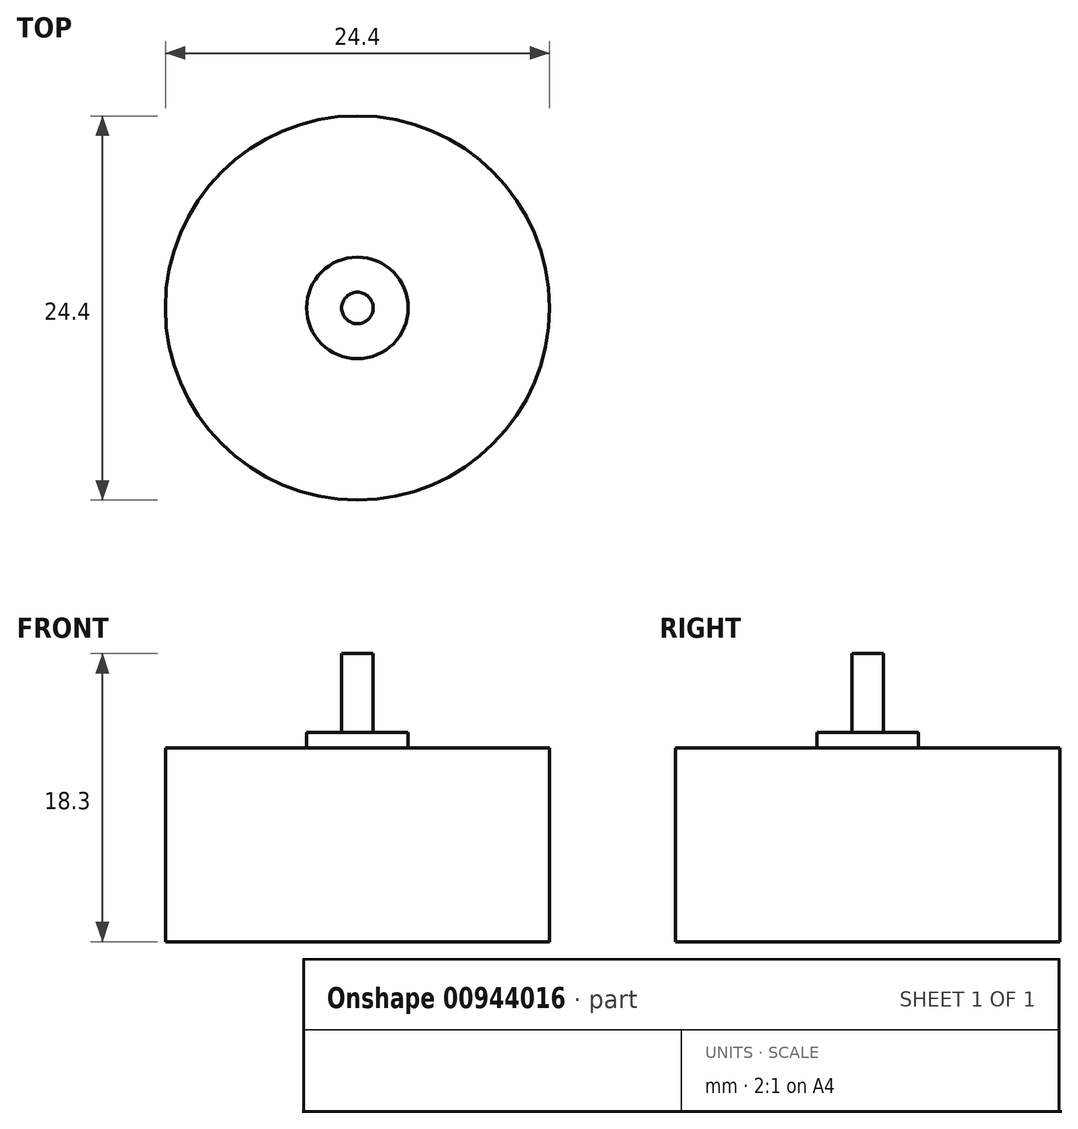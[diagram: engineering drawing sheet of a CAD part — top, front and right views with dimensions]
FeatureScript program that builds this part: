
annotation { "Feature Type Name" : "Feature", "Feature Type Description" : "" }
export const myFeature = defineFeature(function(context is Context, id is Id, definition is map)
    precondition{}
    {
        {
            var Q0;
            Q0=qCreatedBy(makeId("Top.planeOp"),FACE);
            var sketch = newSketch(context, id + "F0", { "sketchPlane" : qUnion([Q0])});
            skCircle(sketch, "E0", {"center": v(0, 0) * mm, "radius": 12.2 * mm});
            skSolve(sketch);
        }
        {
            var Q0;
            Q0=makeQuery(id+"F0.imprint","IMPRINT",FACE,{"disambiguationData":[TD([[makeQuery(id+"F0.imprint","IMPRINT",EDGE,{"derivedFrom":sQuery(id+"F0.wireOp",EDGE,"E0")}),1.0]])]});
            var Q1;
            Q1=sQuery(id+"F0.wireOp",EDGE,"E0");
            extrude(context, id + "F1", {"entities" : qUnion([Q0]), "surfaceEntities" : qUnion([Q1]), "depth" : 12.3 * mm, "offsetDistance" : 25 * mm});
        }
        {
            var Q0;
            Q0=makeQuery(id+"F1.opExtrude","CAP_FACE",FACE,{"disambiguationData":[OSD([sQuery(id+"F0.wireOp",EDGE,"E0")])],"isStart":false});
            var sketch = newSketch(context, id + "F2", { "sketchPlane" : qUnion([Q0])});
            skCircle(sketch, "E1", {"center": v(0, 0) * mm, "radius": 3.23 * mm});
            skSolve(sketch);
        }
        {
            var Q0;
            Q0 = qSketchRegion(id + "F2", true);
            extrude(context, id + "F3", {"entities" : qUnion([Q0]), "operationType" : NewBodyOperationType.ADD, "depth" : 1 * mm, "offsetDistance" : 25 * mm});
        }
        {
            var Q0;
            Q0=makeQuery(id+"F3.opExtrude","CAP_FACE",FACE,{"disambiguationData":[OSD([sQuery(id+"F2.wireOp",EDGE,"E1")])],"isStart":false});
            var sketch = newSketch(context, id + "F4", { "sketchPlane" : qUnion([Q0])});
            skCircle(sketch, "E2", {"center": v(0, 0) * mm, "radius": 1 * mm});
            skSolve(sketch);
        }
        {
            var Q0;
            Q0 = qSketchRegion(id + "F4", true);
            extrude(context, id + "F5", {"entities" : qUnion([Q0]), "operationType" : NewBodyOperationType.ADD, "depth" : 5 * mm, "offsetDistance" : 25 * mm});
        }
    });
